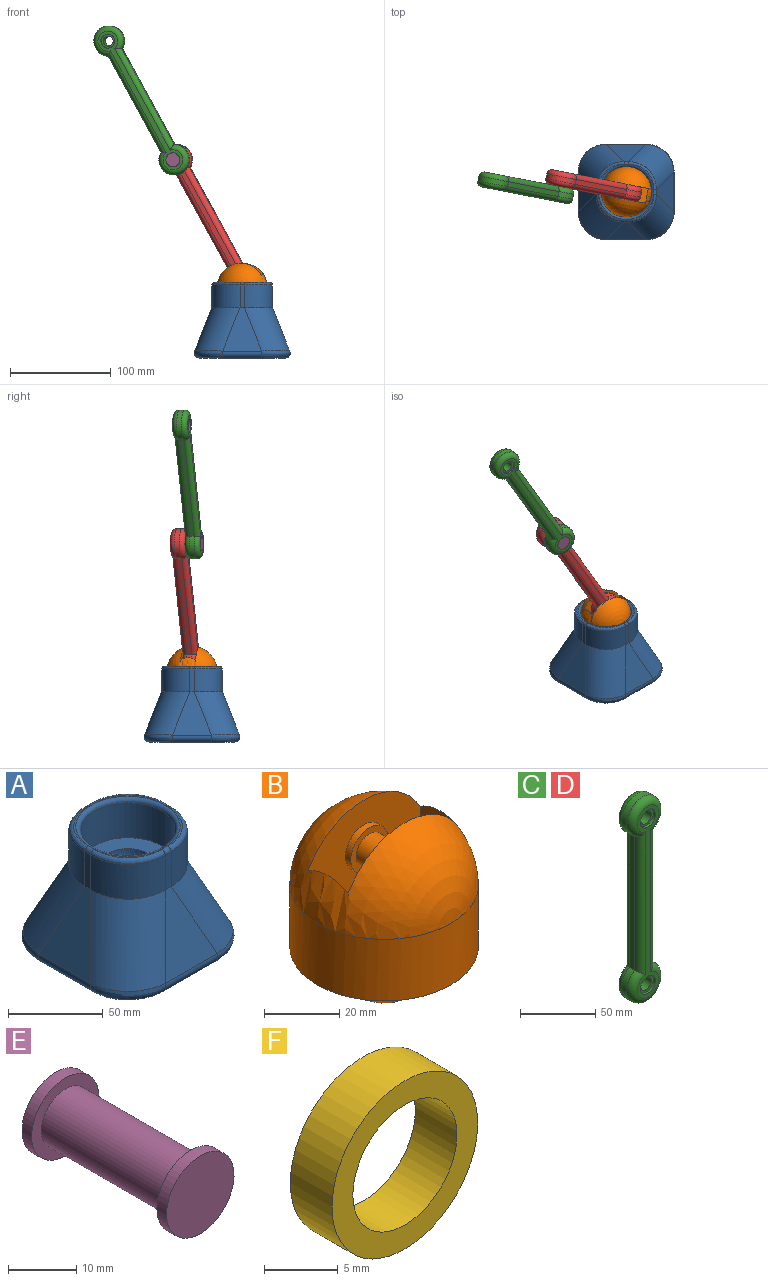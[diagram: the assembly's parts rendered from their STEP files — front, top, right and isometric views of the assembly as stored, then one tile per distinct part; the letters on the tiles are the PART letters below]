
ASSEMBLY  parts=6 mates=6
PART A: 41 faces, bbox 100.2x100.2x75 mm
  f0: plane 27.5x27.5mm, normal (0,0,1), area 30.8mm2, adj f32,f33,f34,f35
  f1: plane 27.5x27.5mm, normal (0,0,1), area 30.8mm2, adj f32,f34,f36,f38
  f2: plane 27.5x27.5mm, normal (0,0,1), area 30.8mm2, adj f32,f38,f39,f40
  f3: plane 85.23x85.23mm, normal (0,0,-1), area 6821.3mm2, adj f8,f9,f10,f11,f13,f15,f17,f19
  f4: plane 43.14x38.81mm, normal (0,-0.93,0.37), area 1001.3mm2, adj f10,f14,f18,f21
  f5: plane 43.14x38.81mm, normal (0.93,0,0.37), area 1001.3mm2, adj f8,f16,f18,f23
  f6: plane 43.14x38.81mm, normal (0,0.93,0.37), area 1001.3mm2, adj f9,f12,f16,f25
  f7: plane 43.14x38.81mm, normal (-0.93,0,0.37), area 1001.3mm2, adj f11,f12,f14,f28
  f8: cylinder r=5mm len=38.81mm, axis (0,-1,0), area 378.6mm2, adj f3,f5,f17,f19
  f9: cylinder r=5mm len=38.81mm, axis (-1,0,0), area 378.6mm2, adj f3,f6,f13,f17
  f10: cylinder r=5mm len=38.81mm, axis (-1,0,0), area 378.6mm2, adj f3,f4,f15,f19
  f11: cylinder r=5mm len=38.81mm, axis (0,-1,0), area 378.6mm2, adj f3,f7,f13,f15
  f12: cylinder r=30mm len=49.81mm, axis (0.35,-0.35,0.87), area 2110.3mm2, adj f6,f7,f13,f26
  f13: bspline ~34.54x34.54mm, area 430.9mm2, adj f3,f9,f11,f12
  f14: cylinder r=30mm len=49.81mm, axis (-0.35,-0.35,-0.87), area 2110.3mm2, adj f4,f7,f15,f20
  f15: bspline ~28.22x28.22mm, area 430.9mm2, adj f3,f10,f11,f14
  f16: cylinder r=30mm len=49.81mm, axis (0.35,0.35,-0.87), area 2110.3mm2, adj f5,f6,f17,f24
  f17: bspline ~28.22x28.22mm, area 430.9mm2, adj f3,f8,f9,f16
  f18: cylinder r=30mm len=49.81mm, axis (-0.35,0.35,0.87), area 2110.3mm2, adj f4,f5,f19,f22
  f19: bspline ~34.54x34.54mm, area 430.9mm2, adj f3,f8,f10,f18
  f20: extruded ~27.85x27.85mm, area 990.3mm2, adj f14,f21,f28,f37
  f21: plane 22.5x4.29mm, normal (0,-1,0), area 96.6mm2, adj f4,f20,f22,f35
  f22: extruded ~27.85x27.85mm, area 990.3mm2, adj f18,f21,f23,f33
  f23: plane 22.5x4.29mm, normal (1,0,0), area 96.6mm2, adj f5,f22,f24,f34
  f24: extruded ~27.85x27.85mm, area 990.3mm2, adj f16,f23,f25,f36
  f25: plane 22.5x4.29mm, normal (0,1,0), area 96.6mm2, adj f6,f24,f26,f38
  f26: extruded ~27.85x27.85mm, area 990.3mm2, adj f12,f25,f28,f40
  f27: cylinder r=25mm len=50mm, axis (0,0,-1), area 3534.3mm2, adj f31,f32
  f28: plane 22.5x4.29mm, normal (-1,0,0), area 96.6mm2, adj f7,f20,f26,f39
  f29: plane 27.5x27.5mm, normal (0,0,1), area 30.8mm2, adj f32,f35,f37,f39
  f30: sphere r=15mm, area 1413.7mm2, adj f31
  f31: plane 50x50mm, normal (0,0,1), area 1256.6mm2, adj f27,f30
  f32: torus R=27.5mm, axis (0,0,1), area 639.3mm2, adj f0,f1,f2,f27,f29
  f33: bspline ~32.23x32.23mm, area 167.2mm2, adj f0,f22,f34,f35
  f34: cylinder r=2.5mm len=4.29mm, axis (0,-1,0), area 16.9mm2, adj f0,f1,f23,f33,f36
  f35: cylinder r=2.5mm len=4.29mm, axis (-1,0,0), area 16.9mm2, adj f0,f21,f29,f33,f37
  f36: bspline ~32.23x32.23mm, area 167.2mm2, adj f1,f24,f34,f38
  f37: bspline ~32.23x32.23mm, area 167.2mm2, adj f20,f29,f35,f39
  f38: cylinder r=2.5mm len=4.29mm, axis (1,0,0), area 16.9mm2, adj f1,f2,f25,f36,f40
  f39: cylinder r=2.5mm len=4.29mm, axis (0,1,0), area 16.9mm2, adj f2,f28,f29,f37,f40
  f40: bspline ~32.23x32.23mm, area 167.2mm2, adj f2,f26,f38,f39
PART B: 14 faces, bbox 50x50x60 mm
  f0: sphere r=25mm, area 3160.2mm2, adj f1,f4,f5,f6,f7
  f1: cylinder r=25mm len=50mm, axis (0,0,1), area 3141.6mm2, adj f0,f2
  f2: plane 50x50mm, normal (0,0,-1), area 1256.6mm2, adj f1,f3
  f3: sphere r=15mm, area 1413.7mm2, adj f2
  f4: plane 28.56x15mm, normal (-1,0,0), area 417.6mm2, adj f0,f5,f7,f8
  f5: plane 42x38.85mm, normal (0,1,0), area 1326mm2, adj f0,f4,f6,f8,f9
  f6: plane 28.56x15mm, normal (1,0,0), area 417.6mm2, adj f0,f5,f7,f8
  f7: plane 42x38.85mm, normal (0,-1,0), area 1326mm2, adj f0,f4,f6,f8,f12
  f8: plane 42x15mm, normal (0,0,1), area 630mm2, adj f4,f5,f6,f7
  f9: cylinder r=7mm len=14mm, axis (0,-1,0), area 88mm2, adj f5,f10
  f10: plane 14x14mm, normal (0,1,0), area 75.4mm2, adj f9,f11
  f11: cylinder r=5mm len=11mm, axis (0,-1,0), area 345.6mm2, adj f10,f13
  f12: cylinder r=7mm len=14mm, axis (0,1,0), area 88mm2, adj f7,f13
  f13: plane 14x14mm, normal (0,-1,0), area 75.4mm2, adj f11,f12
PART C: 24 faces, bbox 32.5x15x167.5 mm
  f0: cylinder r=5mm len=11mm, axis (0,-1,0), area 345.6mm2, adj f19,f22
  f1: cylinder r=5mm len=11mm, axis (0,-1,0), area 345.6mm2, adj f17,f20
  f2: plane 109.02x5mm, normal (1,0,0), area 545.1mm2, adj f3,f5,f8,f12
  f3: cylinder r=15mm len=30mm, axis (0,1,0), area 392.7mm2, adj f2,f4,f9,f13
  f4: plane 109.02x5mm, normal (-1,0,0), area 545.1mm2, adj f3,f5,f11,f15
  f5: cylinder r=15mm len=30mm, axis (0,1,0), area 392.7mm2, adj f2,f4,f10,f14
  f6: plane 155x20mm, normal (0,-1,0), area 896.5mm2, adj f12,f13,f14,f15,f16,f18
  f7: plane 155x20mm, normal (0,1,0), area 896.5mm2, adj f8,f9,f10,f11,f21,f23
  f8: cylinder r=5mm len=115.64mm, axis (0,0,1), area 874.1mm2, adj f2,f7,f9,f10
  f9: torus R=10mm, axis (0,-1,0), area 558mm2, adj f3,f7,f8,f11
  f10: torus R=10mm, axis (0,-1,0), area 558mm2, adj f5,f7,f8,f11
  f11: cylinder r=5mm len=115.64mm, axis (0,0,-1), area 874.1mm2, adj f4,f7,f9,f10
  f12: cylinder r=5mm len=115.64mm, axis (0,0,-1), area 874.1mm2, adj f2,f6,f13,f14
  f13: torus R=10mm, axis (0,-1,0), area 558mm2, adj f3,f6,f12,f15
  f14: torus R=10mm, axis (0,-1,0), area 558mm2, adj f5,f6,f12,f15
  f15: cylinder r=5mm len=115.64mm, axis (0,0,1), area 874.1mm2, adj f4,f6,f13,f14
  f16: cylinder r=7mm len=14mm, axis (0,-1,0), area 88mm2, adj f6,f17
  f17: plane 14x14mm, normal (0,-1,0), area 75.4mm2, adj f1,f16
  f18: cylinder r=7mm len=14mm, axis (0,-1,0), area 88mm2, adj f6,f19
  f19: plane 14x14mm, normal (0,-1,0), area 75.4mm2, adj f0,f18
  f20: plane 14x14mm, normal (0,1,0), area 75.4mm2, adj f1,f21
  f21: cylinder r=7mm len=14mm, axis (0,1,0), area 88mm2, adj f7,f20
  f22: plane 14x14mm, normal (0,1,0), area 75.4mm2, adj f0,f23
  f23: cylinder r=7mm len=14mm, axis (0,1,0), area 88mm2, adj f7,f22
PART D: same geometry as C
PART E: 7 faces, bbox 14x30x14 mm
  f0: plane 14x14mm, normal (0,1,0), area 75.4mm2, adj f1,f6
  f1: cylinder r=5mm len=26mm, axis (0,1,0), area 816.8mm2, adj f0,f2
  f2: plane 14x14mm, normal (0,-1,0), area 75.4mm2, adj f1,f3
  f3: cylinder r=7mm len=14mm, axis (0,1,0), area 88mm2, adj f2,f4
  f4: plane 14x14mm, normal (0,1,0), area 153.9mm2, adj f3
  f5: plane 14x14mm, normal (0,-1,0), area 153.9mm2, adj f6
  f6: cylinder r=7mm len=14mm, axis (0,1,0), area 88mm2, adj f0,f5
PART F: 4 faces, bbox 14x4x14 mm
  f0: cylinder r=5mm len=10mm, axis (0,-1,0), area 125.7mm2, adj f2,f3
  f1: cylinder r=7mm len=14mm, axis (0,-1,0), area 175.9mm2, adj f2,f3
  f2: plane 14x14mm, normal (0,1,0), area 75.4mm2, adj f0,f1
  f3: plane 14x14mm, normal (0,-1,0), area 75.4mm2, adj f0,f1
PLACE A at identity fixed
PLACE B rot(axis=(0,0,1),169.2deg) t=(-47.95,118.88,70)mm
PLACE C rot(axis=(-0.09,-0.94,-0.34),31.1deg) t=(-137.42,78.24,127.42)mm
PLACE D rot(axis=(0.09,1,-0.02),151deg) t=(108.22,46.49,266.07)mm
PLACE E rot(axis=(-0.09,-0.94,-0.34),31.1deg) t=(-253.85,56.04,66.32)mm
PLACE F rot(axis=(0.96,-0.09,0.25),177.3deg) t=(-282.96,146.44,40.89)mm
MATE revolute B.f9 <-> D.f1  axis (0.19,0.98,0) through (48.97,44.6,78.85)mm
MATE planar B.f1 <-> A.f27  axis (0,0,-1) through (50,50,50)mm
MATE fastened F.f0 <-> D.f0  axis (0.19,0.98,0) through (-15.63,56.96,196.74)mm
MATE revolute E.f1 <-> C.f0  axis (0.19,0.98,0) through (-18.45,42.23,196.74)mm
MATE fastened E.f1 <-> D.f0  axis (-0.19,-0.98,0) through (-13.56,67.77,196.74)mm
MATE ball B.f1 <-> A.f27  axis (0,0,1) through (50,50,50)mm
